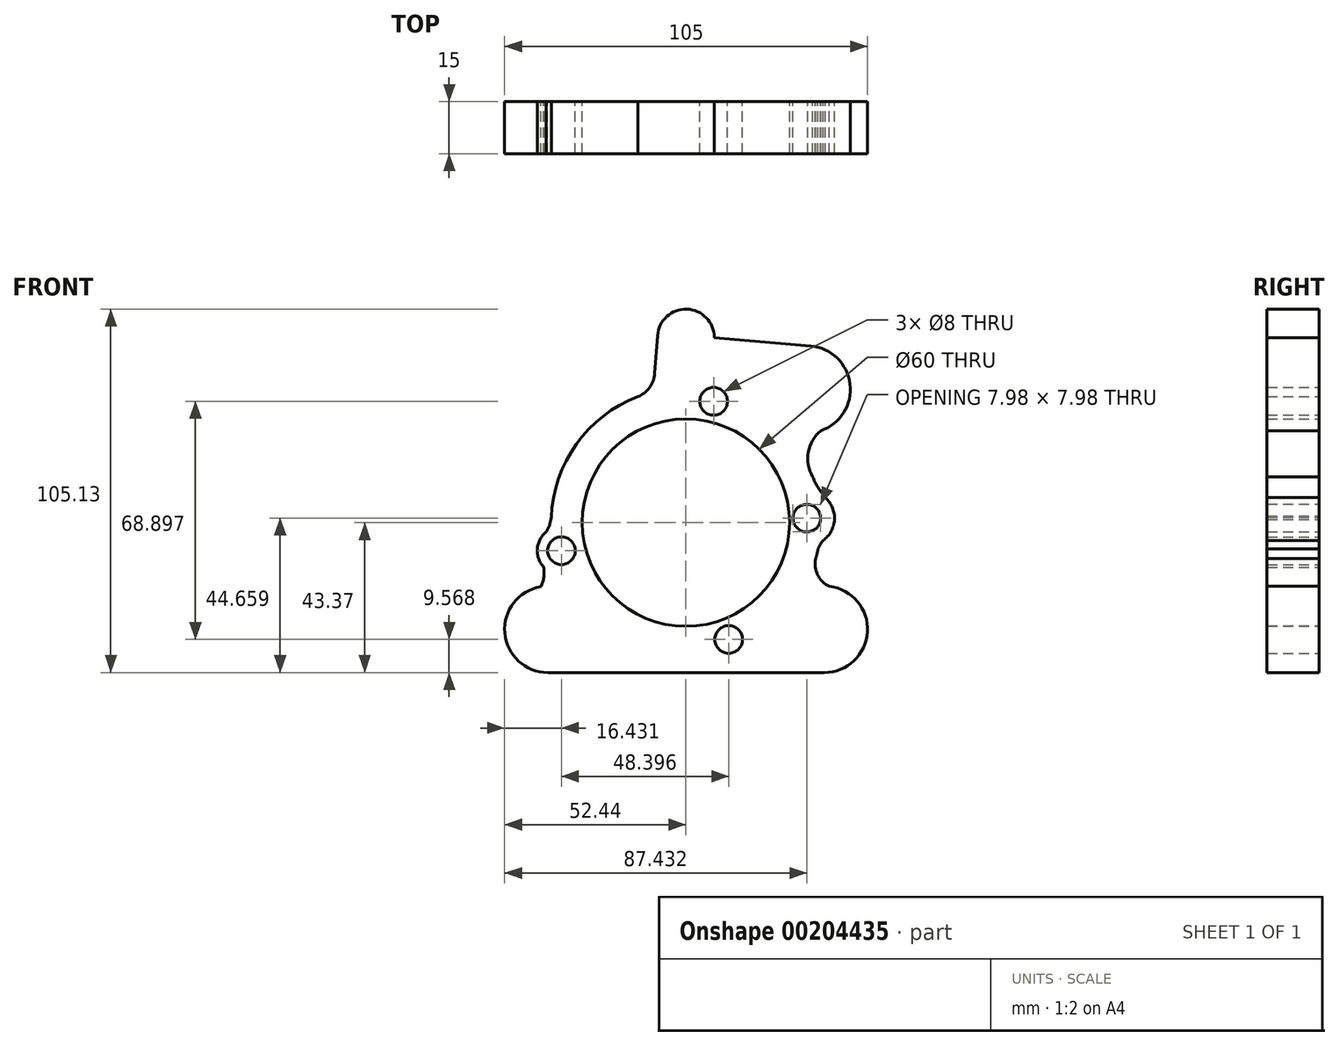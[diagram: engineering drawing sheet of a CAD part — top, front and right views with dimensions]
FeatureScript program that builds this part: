
annotation { "Feature Type Name" : "Feature", "Feature Type Description" : "" }
export const myFeature = defineFeature(function(context is Context, id is Id, definition is map)
    precondition{}
    {
        {
            var Q0;
            Q0=qCreatedBy(makeId("Front.planeOp"),FACE);
            var sketch = newSketch(context, id + "F0", { "sketchPlane" : qUnion([Q0])});
            skCircle(sketch, "E0", {"center": v(0, 0) * mm, "radius": 30 * mm});
            skArc(sketch, "E1", {"start": v(-13.91, 36.43) * mm, "mid": v(-31.69, 22.73) * mm, "end": v(-38.96, 1.5) * mm});
            skLineSegment(sketch, "E2", {"start": v(-29.14, -6.8) * mm, "end": v(-29.22, -6.81) * mm, "construction": true});
            skLineSegment(sketch, "E3", {"start": v(10.32, -28.17) * mm, "end": v(12.39, -33.8) * mm, "construction": true});
            skArc(sketch, "E4", {"start": v(38.94, 1.97) * mm, "mid": v(31, 1.15) * mm, "end": v(38.98, 0.92) * mm});
            skCircle(sketch, "E5", {"center": v(-36, -8.13) * mm, "radius": 4 * mm});
            skCircle(sketch, "E6", {"center": v(8.02, 35.1) * mm, "radius": 4 * mm});
            skCircle(sketch, "E7", {"center": v(12.39, -33.8) * mm, "radius": 4 * mm});
            skArc(sketch, "E8", {"start": v(-41.99, -18.54) * mm, "mid": v(-52.4, -31.9) * mm, "end": v(-39.94, -43.37) * mm});
            skArc(sketch, "E9", {"start": v(40.06, -43.37) * mm, "mid": v(52.54, -31.58) * mm, "end": v(41.49, -18.45) * mm});
            skLineSegment(sketch, "E10", {"start": v(-39.94, -43.37) * mm, "end": v(40.06, -43.37) * mm});
            skArc(sketch, "E11", {"start": v(8.22, 53.54) * mm, "mid": v(0.3, 61.75) * mm, "end": v(-8.2, 54.15) * mm});
            skArc(sketch, "E12", {"start": v(39.08, 26.61) * mm, "mid": v(47.51, 40.06) * mm, "end": v(36.1, 51.1) * mm});
            skArc(sketch, "E13", {"start": v(39.71, -5.17) * mm, "mid": v(42.99, 0.87) * mm, "end": v(40.38, 7.22) * mm});
            skArc(sketch, "E14", {"start": v(-40.44, -2.7) * mm, "mid": v(-43, -7.64) * mm, "end": v(-41.14, -12.89) * mm});
            skArc(sketch, "E15", {"start": v(-42.17, -4.8) * mm, "mid": v(-40, -1.94) * mm, "end": v(-38.96, 1.5) * mm});
            skArc(sketch, "E16", {"start": v(-41.99, -18.54) * mm, "mid": v(-41.1, -15.78) * mm, "end": v(-41.14, -12.89) * mm});
            skArc(sketch, "E17", {"start": v(37.58, -10.4) * mm, "mid": v(38.1, -15.12) * mm, "end": v(41.49, -18.45) * mm});
            skArc(sketch, "E18", {"start": v(39.71, -5.17) * mm, "mid": v(38.88, -6.34) * mm, "end": v(38.24, -7.62) * mm});
            skArc(sketch, "E19", {"start": v(42.73, 28.58) * mm, "mid": v(36, 22.36) * mm, "end": v(36.68, 13.22) * mm});
            skArc(sketch, "E20", {"start": v(36.68, 13.22) * mm, "mid": v(38.29, 10.07) * mm, "end": v(40.38, 7.22) * mm});
            skLineSegment(sketch, "E21", {"start": v(8.22, 53.54) * mm, "end": v(36.1, 51.1) * mm});
            skLineSegment(sketch, "E22", {"start": v(-8.2, 54.15) * mm, "end": v(-9, 43.2) * mm});
            skArc(sketch, "E23", {"start": v(-13.91, 36.43) * mm, "mid": v(-10.5, 39.12) * mm, "end": v(-9, 43.2) * mm});
            skLineSegment(sketch, "E24.trimOffspring", {"start": v(7.13, 31.2) * mm, "end": v(8.02, 35.1) * mm, "construction": true});
            skArc(sketch, "E25.trimOffspring", {"start": v(37.58, -10.4) * mm, "mid": v(37.94, -9.02) * mm, "end": v(38.24, -7.62) * mm});
            skArc(sketch, "E26.trimOffspring", {"start": v(38.98, 0.92) * mm, "mid": v(38.97, 1.45) * mm, "end": v(38.94, 1.97) * mm});
            skSolve(sketch);
        }
        {
            var Q0;
            Q0 = qSketchRegion(id + "F0", true);
            extrude(context, id + "F1", {"entities" : qUnion([Q0]), "depth" : 15 * mm});
        }
    });
